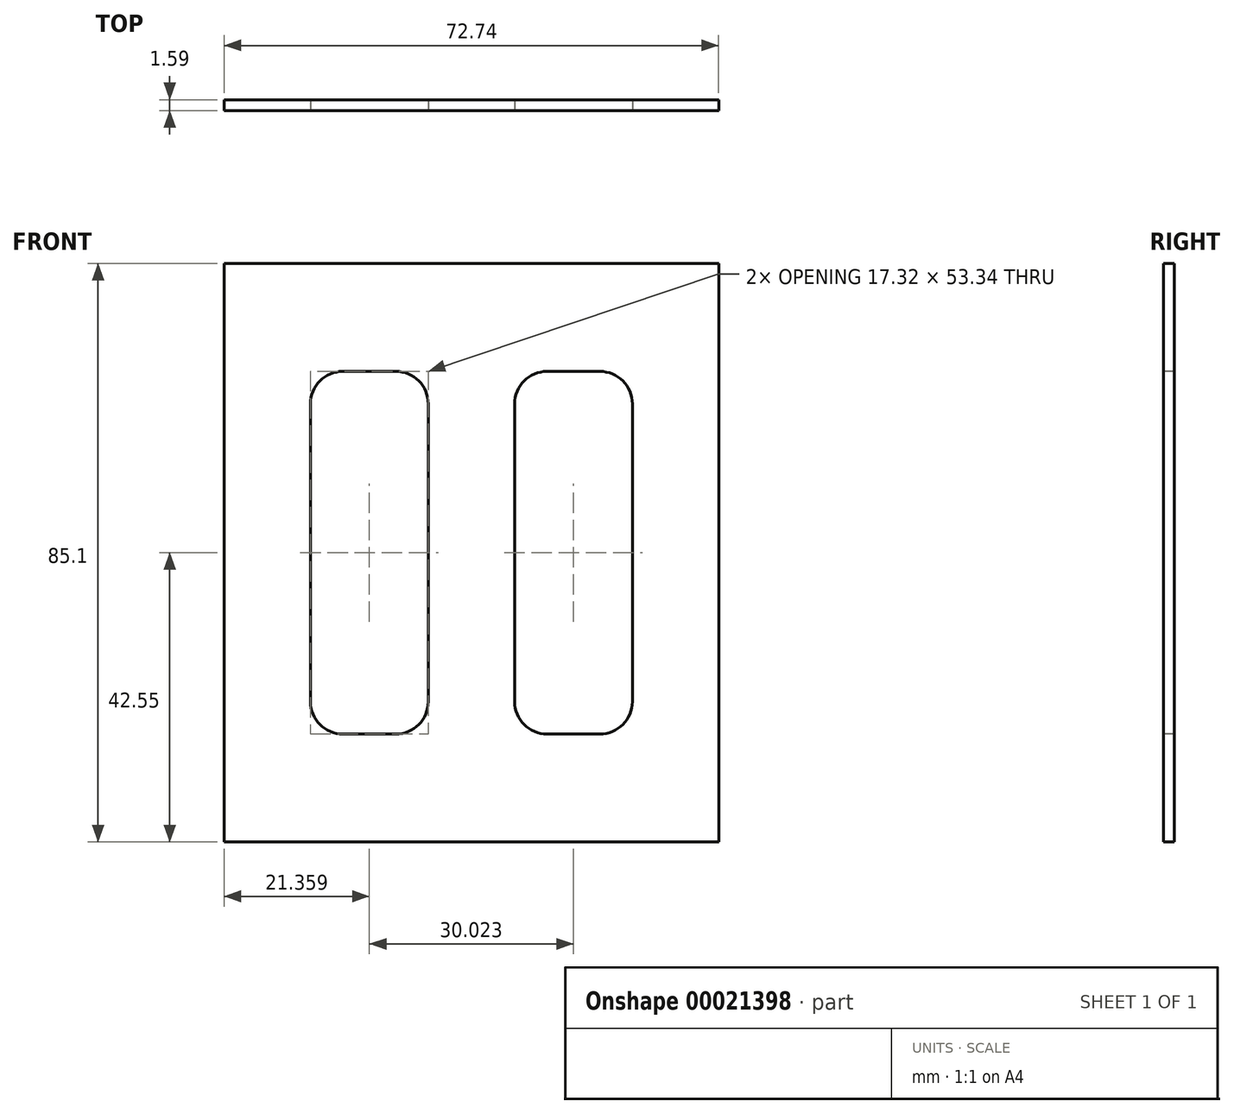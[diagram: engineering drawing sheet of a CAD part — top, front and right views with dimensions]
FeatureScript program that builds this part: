
annotation { "Feature Type Name" : "Feature", "Feature Type Description" : "" }
export const myFeature = defineFeature(function(context is Context, id is Id, definition is map)
    precondition{}
    {
        {
            var Q0;
            Q0=qCreatedBy(makeId("Front.planeOp"),FACE);
            var sketch = newSketch(context, id + "F0", { "sketchPlane" : qUnion([Q0])});
            skLineSegment(sketch, "E0.rect.bottom", {"start": v(36.37, 42.55) * mm, "end": v(-36.37, 42.55) * mm});
            skLineSegment(sketch, "E0.rect.top", {"start": v(36.37, -42.55) * mm, "end": v(-36.37, -42.55) * mm});
            skLineSegment(sketch, "E0.rect.left", {"start": v(36.37, 42.55) * mm, "end": v(36.37, -42.54) * mm});
            skLineSegment(sketch, "E0.rect.right", {"start": v(-36.37, 42.55) * mm, "end": v(-36.37, -42.54) * mm});
            skPoint(sketch, "E0.rect.middle", {"position": v(0, 0) * mm});
            skLineSegment(sketch, "E1.bottom", {"start": v(-23.67, 26.67) * mm, "end": v(-6.35, 26.67) * mm});
            skLineSegment(sketch, "E1.top", {"start": v(-23.67, -26.67) * mm, "end": v(-6.35, -26.67) * mm});
            skLineSegment(sketch, "E1.left", {"start": v(-23.67, 26.67) * mm, "end": v(-23.67, -26.67) * mm});
            skLineSegment(sketch, "E1.right", {"start": v(-6.35, 26.67) * mm, "end": v(-6.35, -26.67) * mm});
            skLineSegment(sketch, "E2.bottom", {"start": v(6.35, 26.67) * mm, "end": v(23.67, 26.67) * mm});
            skLineSegment(sketch, "E2.top", {"start": v(6.35, -26.67) * mm, "end": v(23.67, -26.67) * mm});
            skLineSegment(sketch, "E2.left", {"start": v(6.35, 26.67) * mm, "end": v(6.35, -26.67) * mm});
            skLineSegment(sketch, "E2.right", {"start": v(23.67, 26.67) * mm, "end": v(23.67, -26.67) * mm});
            skLineSegment(sketch, "E3", {"start": v(0, 0) * mm, "end": v(0, 42.55) * mm});
            skLineSegment(sketch, "E4", {"start": v(0, 0) * mm, "end": v(36.37, 0) * mm});
            skSolve(sketch);
        }
        {
            var Q0;
            {var subQ10=sQuery(id+"F0.wireOp",EDGE,"E0.rect.top");Q0=makeQuery(id+"F0.imprint","IMPRINT",FACE,{"disambiguationData":[TD([[makeQuery(id+"F0.imprint","IMPRINT",EDGE,{"derivedFrom":subQ10}),-1.0]])]});}
            var Q1;
            {var subQ4=sQuery(id+"F0.wireOp",EDGE,"E2.bottom");Q1=makeQuery(id+"F0.imprint","IMPRINT",FACE,{"disambiguationData":[TD([[makeQuery(id+"F0.imprint","IMPRINT",EDGE,{"derivedFrom":subQ4}),1.0]])]});}
            extrude(context, id + "F1", {"entities" : qUnion([Q0, Q1]), "oppositeDirection" : true, "depth" : 1.59 * mm});
        }
        {
            var Q0;
            Q0=makeQuery(id+"F1.opExtrude","SWEPT_EDGE",EDGE,{"disambiguationData":[OSD([sQuery(id+"F0.wireOp",EDGE,"E2.bottom"),sQuery(id+"F0.wireOp",EDGE,"E2.left")])]});
            fillet(context, id + "F2", {"entities" : qUnion([Q0]), "radius" : 4.78 * mm, "tangentPropagation" : true, "allowEdgeOverflow" : false});
        }
        {
            var Q0;
            Q0=makeQuery(id+"F1.opExtrude","SWEPT_EDGE",EDGE,{"disambiguationData":[OSD([sQuery(id+"F0.wireOp",EDGE,"E1.bottom"),sQuery(id+"F0.wireOp",EDGE,"E1.right")])]});
            var Q1;
            Q1=makeQuery(id+"F1.opExtrude","SWEPT_EDGE",EDGE,{"disambiguationData":[OSD([sQuery(id+"F0.wireOp",EDGE,"E1.bottom"),sQuery(id+"F0.wireOp",EDGE,"E1.left")])]});
            var Q2;
            Q2=makeQuery(id+"F1.opExtrude","SWEPT_EDGE",EDGE,{"disambiguationData":[OSD([sQuery(id+"F0.wireOp",EDGE,"E1.top"),sQuery(id+"F0.wireOp",EDGE,"E1.left")])]});
            var Q3;
            Q3=makeQuery(id+"F1.opExtrude","SWEPT_EDGE",EDGE,{"disambiguationData":[OSD([sQuery(id+"F0.wireOp",EDGE,"E1.top"),sQuery(id+"F0.wireOp",EDGE,"E1.right")])]});
            fillet(context, id + "F3", {"entities" : qUnion([Q0, Q1, Q2, Q3]), "radius" : 4.78 * mm, "tangentPropagation" : true, "allowEdgeOverflow" : false});
        }
        {
            var Q0;
            Q0=makeQuery(id+"F1.opExtrude","SWEPT_EDGE",EDGE,{"disambiguationData":[OSD([sQuery(id+"F0.wireOp",EDGE,"E2.top"),sQuery(id+"F0.wireOp",EDGE,"E2.right")])]});
            var Q1;
            Q1=makeQuery(id+"F1.opExtrude","SWEPT_EDGE",EDGE,{"disambiguationData":[OSD([sQuery(id+"F0.wireOp",EDGE,"E2.top"),sQuery(id+"F0.wireOp",EDGE,"E2.left")])]});
            var Q2;
            Q2=makeQuery(id+"F1.opExtrude","SWEPT_EDGE",EDGE,{"disambiguationData":[OSD([sQuery(id+"F0.wireOp",EDGE,"E2.bottom"),sQuery(id+"F0.wireOp",EDGE,"E2.right")])]});
            fillet(context, id + "F4", {"entities" : qUnion([Q0, Q1, Q2]), "radius" : 4.78 * mm, "tangentPropagation" : true, "allowEdgeOverflow" : false});
        }
    });
